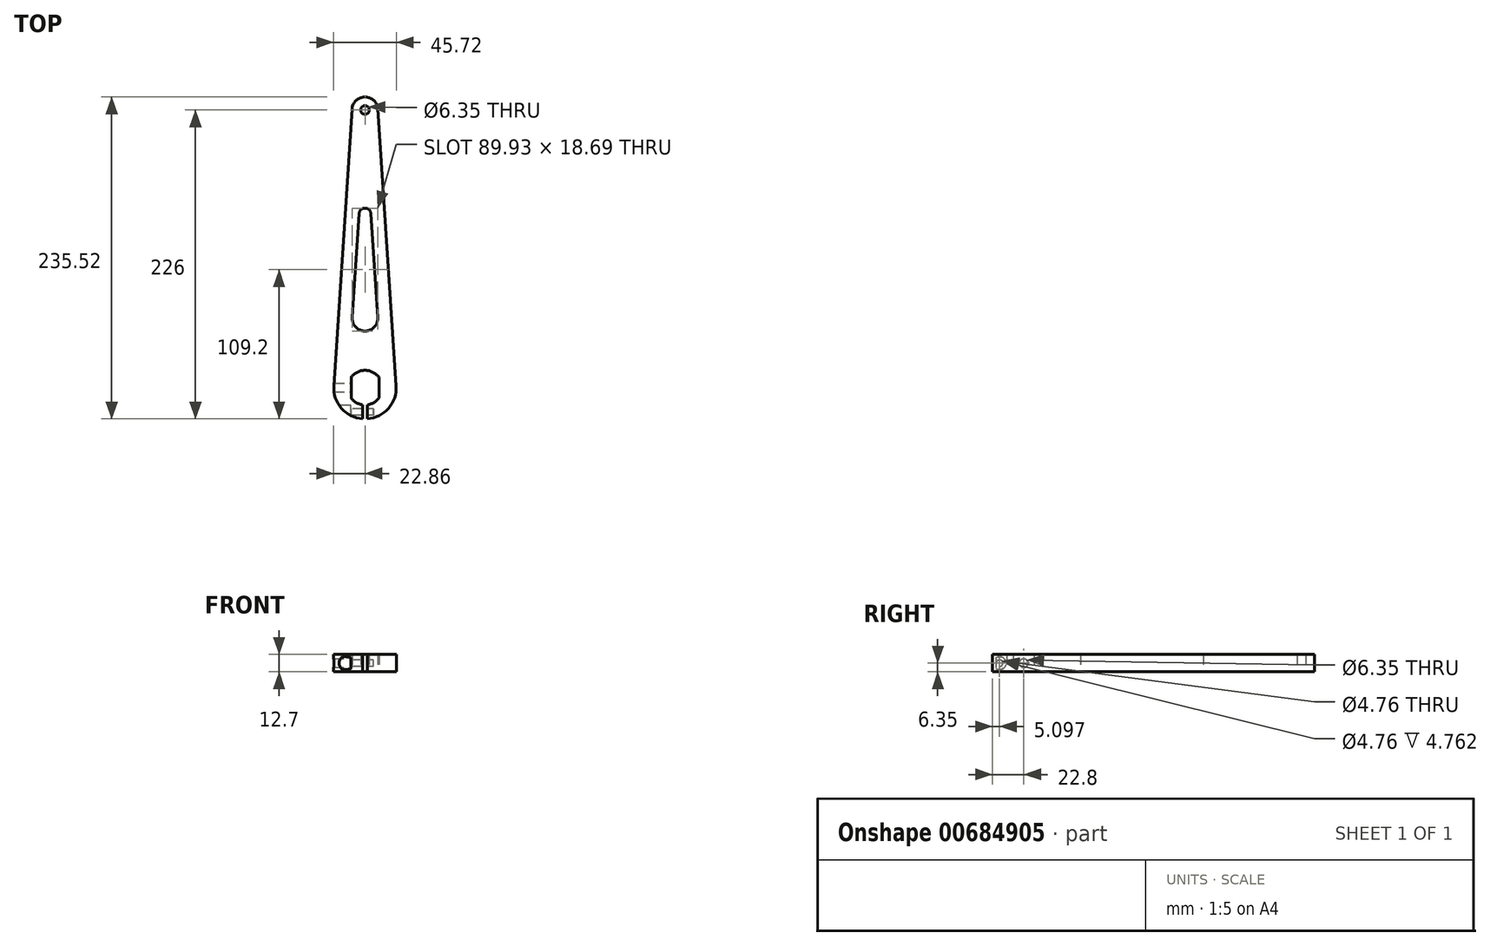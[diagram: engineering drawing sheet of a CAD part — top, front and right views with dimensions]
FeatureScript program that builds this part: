
annotation { "Feature Type Name" : "Feature", "Feature Type Description" : "" }
export const myFeature = defineFeature(function(context is Context, id is Id, definition is map)
    precondition{}
    {
        {
            var Q0;
            Q0=qCreatedBy(makeId("Top.planeOp"),FACE);
            var sketch = newSketch(context, id + "F0", { "sketchPlane" : qUnion([Q0])});
            skLineSegment(sketch, "E0", {"start": v(0, 220.9) * mm, "end": v(0, -303.4) * mm, "construction": true});
            skLineSegment(sketch, "E1", {"start": v(-22.81, 1.5) * mm, "end": v(-9.5, 203.83) * mm});
            skCircle(sketch, "E2", {"center": v(0, 203.2) * mm, "radius": 3.18 * mm});
            skArc(sketch, "E3.0", {"start": v(9.5, 203.83) * mm, "mid": v(0, 212.73) * mm, "end": v(-9.5, 203.83) * mm});
            skArc(sketch, "E4.0", {"start": v(-22.81, 1.5) * mm, "mid": v(-17.22, -15.04) * mm, "end": v(-1.59, -22.8) * mm});
            skLineSegment(sketch, "E5.MirrorCS", {"start": v(22.81, 1.5) * mm, "end": v(9.5, 203.83) * mm});
            skArc(sketch, "E6", {"start": v(-9.35, 51.41) * mm, "mid": v(0, 41.43) * mm, "end": v(9.35, 51.41) * mm});
            skLineSegment(sketch, "E7", {"start": v(9.35, 51.41) * mm, "end": v(4.36, 127.29) * mm});
            skArc(sketch, "E8", {"start": v(4.36, 127.29) * mm, "mid": v(0, 131.37) * mm, "end": v(-4.36, 127.29) * mm});
            skLineSegment(sketch, "E9.MirrorCS", {"start": v(-9.35, 51.41) * mm, "end": v(-4.36, 127.29) * mm});
            skArc(sketch, "E10", {"start": v(10.16, 7.62) * mm, "mid": v(0, 12.7) * mm, "end": v(-10.16, 7.62) * mm});
            skLineSegment(sketch, "E11", {"start": v(-10.16, 7.62) * mm, "end": v(-10.16, -7.62) * mm});
            skLineSegment(sketch, "E12.MirrorCS", {"start": v(10.16, 7.62) * mm, "end": v(10.16, -7.62) * mm});
            skArc(sketch, "E13.trimOffspring", {"start": v(-10.16, -7.62) * mm, "mid": v(-6.38, -10.98) * mm, "end": v(-1.59, -12.6) * mm});
            skLineSegment(sketch, "E14", {"start": v(-1.59, -12.6) * mm, "end": v(-1.59, -22.8) * mm});
            skLineSegment(sketch, "E15.MirrorCS", {"start": v(1.59, -12.6) * mm, "end": v(1.59, -22.8) * mm});
            skArc(sketch, "E16.trimOffspring", {"start": v(1.59, -12.6) * mm, "mid": v(6.38, -10.98) * mm, "end": v(10.16, -7.62) * mm});
            skArc(sketch, "E17.trimOffspring", {"start": v(1.59, -22.8) * mm, "mid": v(17.22, -15.04) * mm, "end": v(22.81, 1.5) * mm});
            skSolve(sketch);
        }
        {
            var Q0;
            Q0 = qSketchRegion(id + "F0", true);
            extrude(context, id + "F1", {"entities" : qUnion([Q0]), "depth" : 12.7 * mm, "offsetDistance" : 25.4 * mm});
        }
        {
            var Q0;
            Q0=makeQuery(id+"F1.opExtrude","SWEPT_FACE",FACE,{"disambiguationData":[OSD([sQuery(id+"F0.wireOp",EDGE,"E11")])]});
            var sketch = newSketch(context, id + "F2", { "sketchPlane" : qUnion([Q0])});
            skCircle(sketch, "E18", {"center": v(0, 6.35) * mm, "radius": 3.18 * mm});
            skLineSegment(sketch, "E19", {"start": v(0, 0) * mm, "end": v(0, 12.7) * mm, "construction": true});
            skSolve(sketch);
        }
        {
            var Q0;
            Q0 = qSketchRegion(id + "F2", true);
            extrude(context, id + "F3", {"entities" : qUnion([Q0]), "operationType" : NewBodyOperationType.REMOVE, "oppositeDirection" : true, "depth" : 25.4 * mm, "offsetDistance" : 25.4 * mm});
        }
        {
            var Q0;
            Q0=qCreatedBy(makeId("Right.planeOp"),FACE);
            var sketch = newSketch(context, id + "F4", { "sketchPlane" : qUnion([Q0])});
            skLineSegment(sketch, "E20", {"start": v(-22.8, 12.7) * mm, "end": v(-12.6, 12.7) * mm, "construction": true});
            skLineSegment(sketch, "E21", {"start": v(-17.7, 12.7) * mm, "end": v(-17.7, 0) * mm, "construction": true});
            skCircle(sketch, "E22", {"center": v(-17.7, 6.35) * mm, "radius": 2.38 * mm});
            skSolve(sketch);
        }
        {
            var Q0;
            Q0 = qSketchRegion(id + "F4", true);
            var Q1;
            Q1 = qConstructionFilter(qBodyType(qCreatedBy(id + "F4" ,EDGE), BodyType.WIRE), ConstructionObject.NO);
            extrude(context, id + "F5", {"entities" : qUnion([Q0]), "operationType" : NewBodyOperationType.REMOVE, "surfaceEntities" : qUnion([Q1]), "depth" : 6.35 * mm, "offsetDistance" : 25.4 * mm, "hasSecondDirection" : true, "secondDirectionBound" : BoundingType.THROUGH_ALL, "secondDirectionOppositeDirection" : true, "secondDirectionDepth" : 25.4 * mm});
        }
        {
            var Q0;
            Q0=makeQuery(id+"F1.opExtrude","SWEPT_FACE",FACE,{"disambiguationData":[OSD([sQuery(id+"F0.wireOp",EDGE,"E14")])]});
            cPlane(context, id + "F6", {"entities" : qUnion([Q0]), "cplaneType" : CPlaneType.OFFSET, "offset" : 19.05 * mm, "oppositeDirection" : true, "width" : 152.4 * mm, "height" : 152.4 * mm});
        }
        {
            var Q0;
            Q0=qCreatedBy(id+"F6.planeOp",FACE);
            var sketch = newSketch(context, id + "F7", { "sketchPlane" : qUnion([Q0])});
            skCircle(sketch, "E23", {"center": v(-17.7, 6.35) * mm, "radius": 4.76 * mm});
            skSolve(sketch);
        }
        {
            var Q0;
            Q0 = qSketchRegion(id + "F7", true);
            var Q1;
            Q1 = qConstructionFilter(qBodyType(qCreatedBy(id + "F7" ,EDGE), BodyType.WIRE), ConstructionObject.NO);
            extrude(context, id + "F8", {"entities" : qUnion([Q0]), "operationType" : NewBodyOperationType.REMOVE, "surfaceEntities" : qUnion([Q1]), "depth" : 10.16 * mm, "offsetDistance" : 25.4 * mm});
        }
    });
